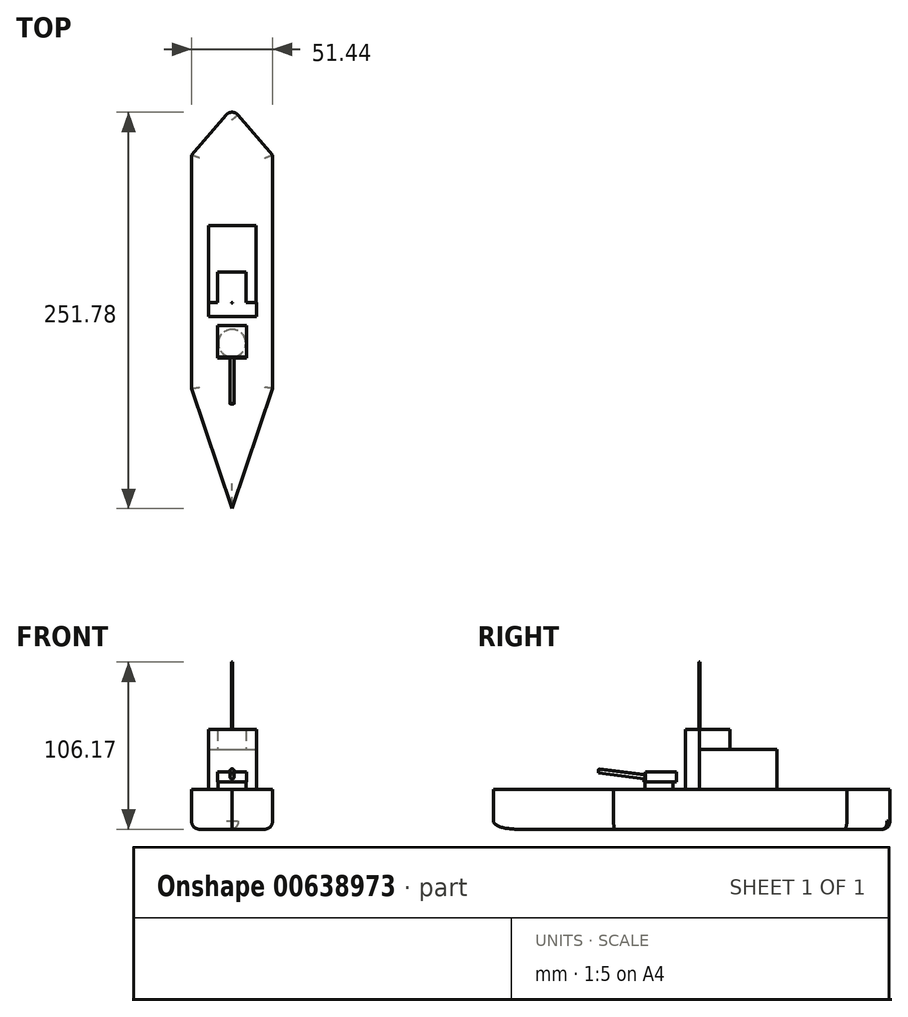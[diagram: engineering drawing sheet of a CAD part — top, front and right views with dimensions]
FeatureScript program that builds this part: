
annotation { "Feature Type Name" : "Feature", "Feature Type Description" : "" }
export const myFeature = defineFeature(function(context is Context, id is Id, definition is map)
    precondition{}
    {
        {
            var Q0;
            Q0=qCreatedBy(makeId("Top.planeOp"),FACE);
            var sketch = newSketch(context, id + "F0", { "sketchPlane" : qUnion([Q0])});
            skLineSegment(sketch, "E0.bottom", {"start": v(-25.72, 74.45) * mm, "end": v(25.72, 74.45) * mm});
            skLineSegment(sketch, "E0.top", {"start": v(-25.72, -73.84) * mm, "end": v(25.72, -73.84) * mm});
            skLineSegment(sketch, "E0.left", {"start": v(-25.72, 74.45) * mm, "end": v(-25.72, -73.84) * mm});
            skLineSegment(sketch, "E0.right", {"start": v(25.72, 74.45) * mm, "end": v(25.72, -73.84) * mm});
            skSolve(sketch);
        }
        {
            var Q0;
            Q0=qSketchRegion(id+"F0",true);
            extrude(context, id + "F1", {"entities" : qUnion([Q0]), "depth" : 25.4 * mm, "offsetDistance" : 25.4 * mm});
        }
        {
            var Q0;
            Q0=qCreatedBy(makeId("Top.planeOp"),FACE);
            var sketch = newSketch(context, id + "F2", { "sketchPlane" : qUnion([Q0])});
            skLineSegment(sketch, "E1", {"start": v(-25.72, -73.84) * mm, "end": v(0, -150.15) * mm});
            skLineSegment(sketch, "E2", {"start": v(0, -150.15) * mm, "end": v(25.72, -73.84) * mm});
            skLineSegment(sketch, "E3", {"start": v(25.72, -73.84) * mm, "end": v(-25.72, -73.84) * mm});
            skSolve(sketch);
        }
        {
            var Q0;
            Q0=qSketchRegion(id+"F2",true);
            extrude(context, id + "F3", {"entities" : qUnion([Q0]), "operationType" : NewBodyOperationType.ADD, "depth" : 25.4 * mm, "offsetDistance" : 25.4 * mm});
        }
        {
            var Q0;
            Q0=makeQuery(id+"F3.opExtrude","CAP_EDGE",EDGE,{"disambiguationData":[OSD([sQuery(id+"F2.wireOp",EDGE,"E2")])],"isStart":true});
            var Q1;
            Q1=makeQuery(id+"F1.opExtrude","CAP_EDGE",EDGE,{"disambiguationData":[OSD([sQuery(id+"F0.wireOp",EDGE,"E0.right")])],"isStart":true});
            var Q2;
            Q2=makeQuery(id+"F3.opExtrude","CAP_EDGE",EDGE,{"disambiguationData":[OSD([sQuery(id+"F2.wireOp",EDGE,"E1")])],"isStart":true});
            var Q3;
            Q3=makeQuery(id+"F1.opExtrude","CAP_EDGE",EDGE,{"disambiguationData":[OSD([sQuery(id+"F0.wireOp",EDGE,"E0.left")])],"isStart":true});
            fillet(context, id + "F4", {"entities" : qUnion([Q0, Q1, Q2, Q3]), "radius" : 5.08 * mm, "tangentPropagation" : true, "allowEdgeOverflow" : false});
        }
        {
            var Q0;
            Q0=qCreatedBy(makeId("Top.planeOp"),FACE);
            var sketch = newSketch(context, id + "F5", { "sketchPlane" : qUnion([Q0])});
            skLineSegment(sketch, "E4", {"start": v(-25.71, 74.45) * mm, "end": v(0, 104.42) * mm});
            skLineSegment(sketch, "E5", {"start": v(0, 104.42) * mm, "end": v(25.72, 74.44) * mm});
            skLineSegment(sketch, "E6", {"start": v(25.72, 74.44) * mm, "end": v(-25.71, 74.45) * mm});
            skSolve(sketch);
        }
        {
            var Q0;
            Q0=qSketchRegion(id+"F5",true);
            extrude(context, id + "F6", {"entities" : qUnion([Q0]), "operationType" : NewBodyOperationType.ADD, "depth" : 25.4 * mm, "offsetDistance" : 25.4 * mm});
        }
        {
            var Q0;
            Q0=makeQuery(id+"F6.opExtrude","CAP_EDGE",EDGE,{"disambiguationData":[OSD([sQuery(id+"F5.wireOp",EDGE,"E4")])],"isStart":true});
            fillet(context, id + "F7", {"entities" : qUnion([Q0]), "radius" : 4.9 * mm, "tangentPropagation" : true, "allowEdgeOverflow" : false});
        }
        {
            var Q0;
            Q0=makeQuery(id+"F6.opExtrude","CAP_EDGE",EDGE,{"disambiguationData":[OSD([sQuery(id+"F5.wireOp",EDGE,"E5")])],"isStart":true});
            fillet(context, id + "F8", {"entities" : qUnion([Q0]), "radius" : 5.2 * mm, "tangentPropagation" : true, "allowEdgeOverflow" : false});
        }
        {
            var Q0;
            Q0=makeQuery(id+"F6.boolean.opBoolean","MERGE",FACE,{"derivedFrom":[makeQuery(id+"F3.boolean.opBoolean","MERGE",FACE,{"derivedFrom":[makeQuery(id+"F1.opExtrude","CAP_FACE",FACE,{"disambiguationData":[OSD([sQuery(id+"F0.wireOp",EDGE,"E0.bottom"),sQuery(id+"F0.wireOp",EDGE,"E0.top"),sQuery(id+"F0.wireOp",EDGE,"E0.left"),sQuery(id+"F0.wireOp",EDGE,"E0.right")])],"isStart":false}),makeQuery(id+"F3.opExtrude","CAP_FACE",FACE,{"disambiguationData":[OSD([sQuery(id+"F2.wireOp",EDGE,"E1"),sQuery(id+"F2.wireOp",EDGE,"E2"),sQuery(id+"F2.wireOp",EDGE,"E3")])],"isStart":false})]}),makeQuery(id+"F6.opExtrude","CAP_FACE",FACE,{"disambiguationData":[OSD([sQuery(id+"F5.wireOp",EDGE,"E4"),sQuery(id+"F5.wireOp",EDGE,"E5"),sQuery(id+"F5.wireOp",EDGE,"E6")])],"isStart":false})]});
            var sketch = newSketch(context, id + "F9", { "sketchPlane" : qUnion([Q0])});
            skCircle(sketch, "E7", {"center": v(0, -70.44) * mm, "radius": 6.4 * mm});
            skLineSegment(sketch, "E8.bottom", {"start": v(-15.04, 29.75) * mm, "end": v(15.44, 29.75) * mm});
            skLineSegment(sketch, "E8.top", {"start": v(-15.04, -19.24) * mm, "end": v(15.44, -19.24) * mm});
            skLineSegment(sketch, "E8.left", {"start": v(-15.04, 29.75) * mm, "end": v(-15.04, -19.24) * mm});
            skLineSegment(sketch, "E8.right", {"start": v(15.44, 29.75) * mm, "end": v(15.44, -19.24) * mm});
            skSolve(sketch);
        }
        {
            var Q0;
            Q0=makeQuery(id+"F9.imprint","IMPRINT",FACE,{"disambiguationData":[TD([[makeQuery(id+"F9.imprint","IMPRINT",EDGE,{"derivedFrom":sQuery(id+"F9.wireOp",EDGE,"E8.bottom")}),-1.0]])]});
            var sketch = newSketch(context, id + "F10", { "sketchPlane" : qUnion([Q0])});
            skLineSegment(sketch, "E9.bottom", {"start": v(-15.04, 29.78) * mm, "end": v(15.36, 29.78) * mm});
            skLineSegment(sketch, "E9.top", {"start": v(-15.04, -19.27) * mm, "end": v(15.36, -19.27) * mm});
            skLineSegment(sketch, "E9.left", {"start": v(-15.04, 29.78) * mm, "end": v(-15.04, -19.27) * mm});
            skLineSegment(sketch, "E9.right", {"start": v(15.36, 29.78) * mm, "end": v(15.36, -19.27) * mm});
            skSolve(sketch);
        }
        {
            var Q0;
            Q0=qSketchRegion(id+"F10",true);
            extrude(context, id + "F11", {"entities" : qUnion([Q0]), "operationType" : NewBodyOperationType.ADD, "depth" : 25.4 * mm, "offsetDistance" : 25.4 * mm});
        }
        {
            var Q0;
            Q0=makeQuery(id+"F11.opExtrude","CAP_FACE",FACE,{"disambiguationData":[OSD([sQuery(id+"F10.wireOp",EDGE,"E9.bottom"),sQuery(id+"F10.wireOp",EDGE,"E9.top"),sQuery(id+"F10.wireOp",EDGE,"E9.left"),sQuery(id+"F10.wireOp",EDGE,"E9.right")])],"isStart":false});
            var sketch = newSketch(context, id + "F12", { "sketchPlane" : qUnion([Q0])});
            skCircle(sketch, "E10", {"center": v(0, 21.42) * mm, "radius": 4.66 * mm});
            skSolve(sketch);
        }
        {
            var Q0;
            Q0=makeQuery(id+"F9.imprint","IMPRINT",FACE,{"disambiguationData":[TD([[makeQuery(id+"F9.imprint","IMPRINT",EDGE,{"derivedFrom":sQuery(id+"F9.wireOp",EDGE,"E7")}),-1.0]])]});
            var sketch = newSketch(context, id + "F13", { "sketchPlane" : qUnion([Q0])});
            skLineSegment(sketch, "E11", {"start": v(-15.04, -19.27) * mm, "end": v(15.4, -19.27) * mm});
            skLineSegment(sketch, "E12", {"start": v(15.4, -19.27) * mm, "end": v(15.4, -28.2) * mm});
            skLineSegment(sketch, "E13", {"start": v(15.4, -28.2) * mm, "end": v(-15, -28.2) * mm});
            skLineSegment(sketch, "E14", {"start": v(-15, -28.2) * mm, "end": v(-15.04, -19.27) * mm});
            skSolve(sketch);
        }
        {
            var Q0;
            Q0=makeQuery(id+"F13.imprint","IMPRINT",FACE,{"disambiguationData":[TD([[makeQuery(id+"F13.imprint","IMPRINT",EDGE,{"derivedFrom":sQuery(id+"F13.wireOp",EDGE,"E11")}),-1.0]])]});
            extrude(context, id + "F14", {"entities" : qUnion([Q0]), "operationType" : NewBodyOperationType.ADD, "depth" : 38.1 * mm, "offsetDistance" : 25.4 * mm});
        }
        {
            var Q0;
            Q0=makeQuery(id+"F12.imprint","IMPRINT",FACE,{"disambiguationData":[TD([[makeQuery(id+"F12.imprint","IMPRINT",EDGE,{"derivedFrom":sQuery(id+"F12.wireOp",EDGE,"E10")}),-1.0]])]});
            var sketch = newSketch(context, id + "F15", { "sketchPlane" : qUnion([Q0])});
            skLineSegment(sketch, "E15.bottom", {"start": v(-9.29, 0) * mm, "end": v(8.88, 0) * mm});
            skLineSegment(sketch, "E15.top", {"start": v(-9.29, -19.32) * mm, "end": v(8.88, -19.32) * mm});
            skLineSegment(sketch, "E15.left", {"start": v(-9.29, 0) * mm, "end": v(-9.29, -19.32) * mm});
            skLineSegment(sketch, "E15.right", {"start": v(8.88, 0) * mm, "end": v(8.88, -19.32) * mm});
            skSolve(sketch);
        }
        {
            var Q0;
            Q0=qSketchRegion(id+"F15",true);
            extrude(context, id + "F16", {"entities" : qUnion([Q0]), "operationType" : NewBodyOperationType.ADD, "depth" : 12.7 * mm, "offsetDistance" : 25.4 * mm});
        }
        {
            var Q0;
            Q0=makeQuery(id+"F9.imprint","IMPRINT",FACE,{"disambiguationData":[TD([[makeQuery(id+"F9.imprint","IMPRINT",EDGE,{"derivedFrom":sQuery(id+"F9.wireOp",EDGE,"E7")}),-1.0]])]});
            var sketch = newSketch(context, id + "F17", { "sketchPlane" : qUnion([Q0])});
            skCircle(sketch, "E16", {"center": v(0, -45.04) * mm, "radius": 8.75 * mm});
            skSolve(sketch);
        }
        {
            var Q0;
            Q0=makeQuery(id+"F17.imprint","IMPRINT",FACE,{"disambiguationData":[TD([[makeQuery(id+"F17.imprint","IMPRINT",EDGE,{"derivedFrom":sQuery(id+"F17.wireOp",EDGE,"E16")}),1.0]])]});
            extrude(context, id + "F18", {"entities" : qUnion([Q0]), "operationType" : NewBodyOperationType.ADD, "depth" : 4.57 * mm, "offsetDistance" : 25.4 * mm});
        }
        {
            var Q0;
            Q0=makeQuery(id+"F18.opExtrude","CAP_FACE",FACE,{"disambiguationData":[OSD([sQuery(id+"F17.wireOp",EDGE,"E16")])],"isStart":false});
            var sketch = newSketch(context, id + "F19", { "sketchPlane" : qUnion([Q0])});
            skLineSegment(sketch, "E17.bottom", {"start": v(-9.1, -33.92) * mm, "end": v(9.25, -33.92) * mm});
            skLineSegment(sketch, "E17.top", {"start": v(-9.1, -53.77) * mm, "end": v(9.25, -53.77) * mm});
            skLineSegment(sketch, "E17.left", {"start": v(-9.1, -33.92) * mm, "end": v(-9.1, -53.77) * mm});
            skLineSegment(sketch, "E17.right", {"start": v(9.25, -33.92) * mm, "end": v(9.25, -53.77) * mm});
            skSolve(sketch);
        }
        {
            var Q0;
            Q0=qSketchRegion(id+"F19",true);
            extrude(context, id + "F20", {"entities" : qUnion([Q0]), "operationType" : NewBodyOperationType.ADD, "depth" : 6.6 * mm, "offsetDistance" : 25.4 * mm});
        }
        {
            var Q0;
            Q0=makeQuery(id+"F20.opExtrude","SWEPT_FACE",FACE,{"disambiguationData":[OSD([sQuery(id+"F19.wireOp",EDGE,"E17.left")])]});
            var sketch = newSketch(context, id + "F21", { "sketchPlane" : qUnion([Q0])});
            skLineSegment(sketch, "E18", {"start": v(53.77, 36.58) * mm, "end": v(54.59, 30.14) * mm});
            skLineSegment(sketch, "E19", {"start": v(54.59, 30.14) * mm, "end": v(53.77, 30.03) * mm});
            skLineSegment(sketch, "E20", {"start": v(53.77, 30.03) * mm, "end": v(53.77, 36.58) * mm});
            skSolve(sketch);
        }
        {
            var Q0;
            Q0=qSketchRegion(id+"F21",true);
            extrude(context, id + "F22", {"entities" : qUnion([Q0]), "operationType" : NewBodyOperationType.ADD, "oppositeDirection" : true, "depth" : 18.3 * mm, "offsetDistance" : 25.4 * mm});
        }
        {
            var Q0;
            Q0=makeQuery(id+"F22.opExtrude","SWEPT_FACE",FACE,{"disambiguationData":[OSD([sQuery(id+"F21.wireOp",EDGE,"E18")])]});
            var sketch = newSketch(context, id + "F23", { "sketchPlane" : qUnion([Q0])});
            skCircle(sketch, "E21", {"center": v(0, 26.15) * mm, "radius": 1.34 * mm});
            skSolve(sketch);
        }
        {
            var Q0;
            Q0=makeQuery(id+"F23.imprint","IMPRINT",FACE,{"disambiguationData":[TD([[makeQuery(id+"F23.imprint","IMPRINT",EDGE,{"derivedFrom":sQuery(id+"F23.wireOp",EDGE,"E21")}),1.0]])]});
            extrude(context, id + "F24", {"entities" : qUnion([Q0]), "operationType" : NewBodyOperationType.ADD, "depth" : 29.46 * mm, "offsetDistance" : 25.4 * mm});
        }
        {
            var Q0;
            Q0=makeQuery(id+"F16.boolean.opBoolean","MERGE",FACE,{"derivedFrom":[makeQuery(id+"F14.opExtrude","CAP_FACE",FACE,{"disambiguationData":[OSD([sQuery(id+"F13.wireOp",EDGE,"E11"),sQuery(id+"F13.wireOp",EDGE,"E12"),sQuery(id+"F13.wireOp",EDGE,"E13"),sQuery(id+"F13.wireOp",EDGE,"E14")])],"isStart":false}),makeQuery(id+"F16.opExtrude","CAP_FACE",FACE,{"disambiguationData":[OSD([sQuery(id+"F15.wireOp",EDGE,"E15.bottom"),sQuery(id+"F15.wireOp",EDGE,"E15.top"),sQuery(id+"F15.wireOp",EDGE,"E15.left"),sQuery(id+"F15.wireOp",EDGE,"E15.right")])],"isStart":false})]});
            var sketch = newSketch(context, id + "F25", { "sketchPlane" : qUnion([Q0])});
            skCircle(sketch, "E22", {"center": v(0, -19.33) * mm, "radius": 0.2 * mm});
            skSolve(sketch);
        }
        {
            var Q0;
            Q0=qSketchRegion(id+"F25",true);
            extrude(context, id + "F26", {"entities" : qUnion([Q0]), "operationType" : NewBodyOperationType.ADD, "depth" : 42.67 * mm, "offsetDistance" : 25.4 * mm});
        }
    });
